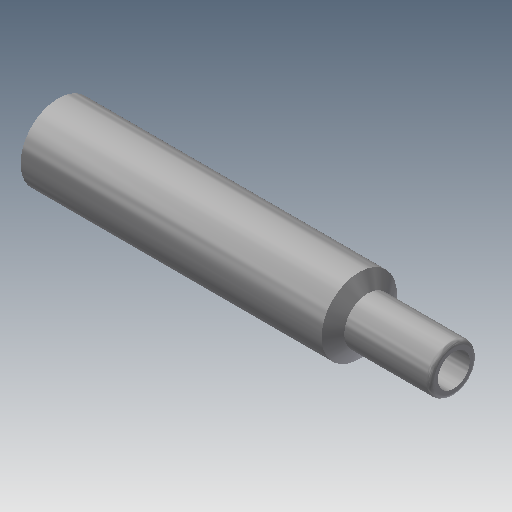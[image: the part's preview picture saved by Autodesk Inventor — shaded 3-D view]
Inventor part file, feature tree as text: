
AUTODESK INVENTOR PART (.ipt)
format: ipt  version: 2021 (Build 250183000, 183)  size: 144,384 bytes
history: native  units: mm
features: other x1, revolve x1, fillet x1, sketch x1
ambient origin geometry x8: Origin, YZ Plane, XZ Plane, XY Plane, X Axis, Y Axis, Z Axis, Center Point
bodies: Body1 (feature_tree)
feature tree (4):
  other  "Sólido2"
  revolve  "Revolución2"  [1 undecoded]
  fillet  "Empalme2"  [1 undecoded]
  sketch  "Boceto1"  dims[d5=140.0mm d9=40.0mm d10=90.0deg d11=2.0mm d13=17.526mm d14=14.0mm]
note: 2 required parameter values undecoded (feature->parameter linkage not recoverable at this tier; creation-order binding heuristic only, values carry confidence <= 0.55)